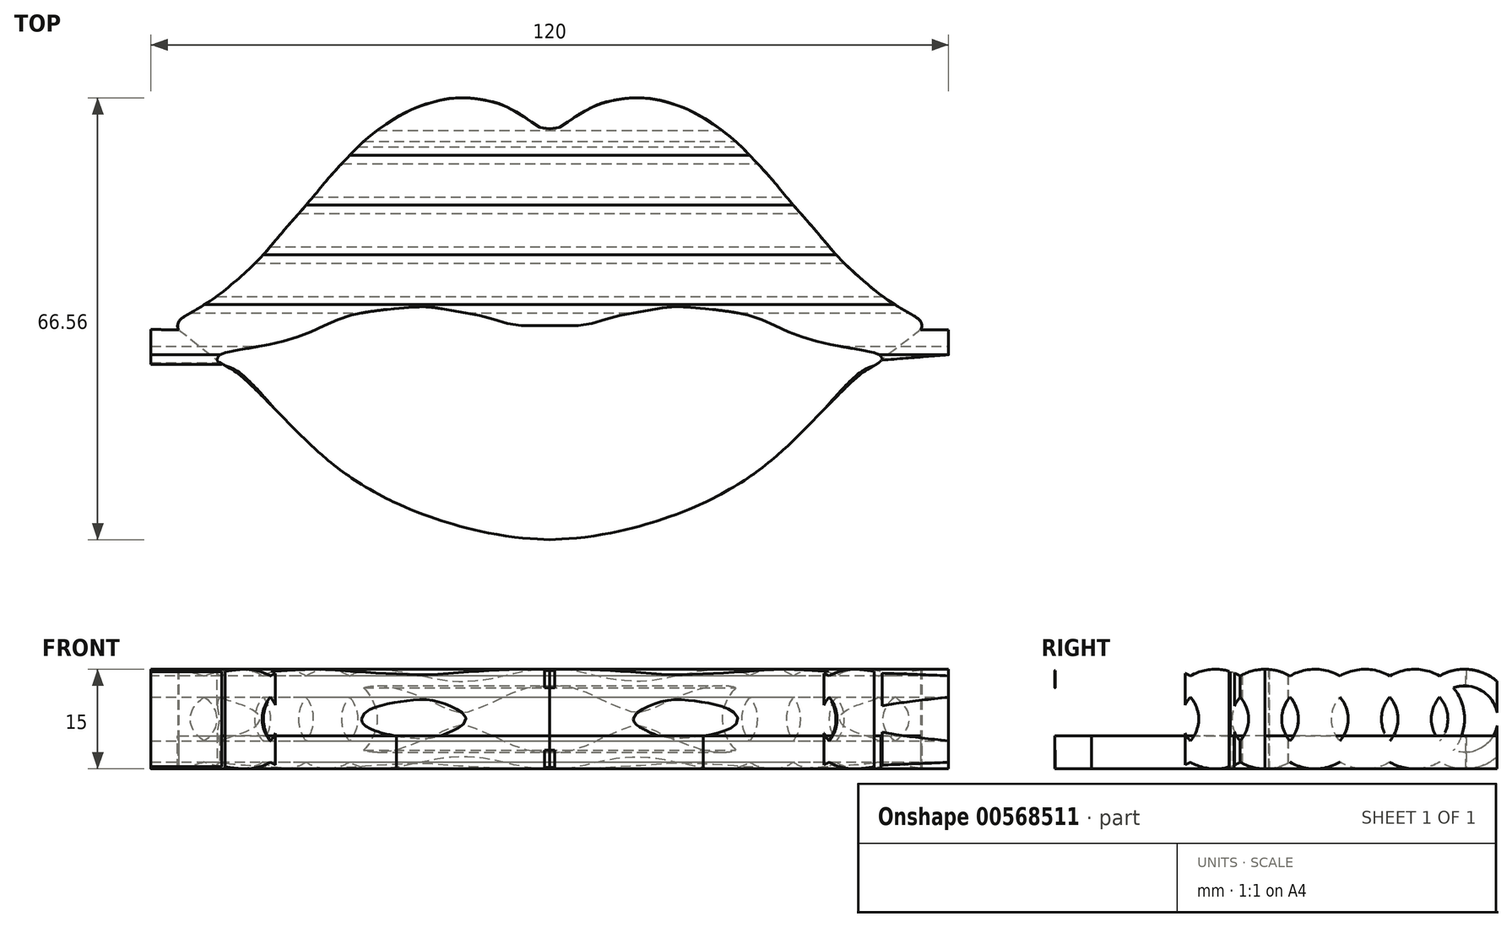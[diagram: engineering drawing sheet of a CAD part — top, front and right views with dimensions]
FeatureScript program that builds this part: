
annotation { "Feature Type Name" : "Feature", "Feature Type Description" : "" }
export const myFeature = defineFeature(function(context is Context, id is Id, definition is map)
    precondition{}
    {
        {
            var Q0;
            Q0=qCreatedBy(makeId("Right.planeOp"),FACE);
            var sketch = newSketch(context, id + "F0", { "sketchPlane" : qUnion([Q0])});
            skLineSegment(sketch, "E0", {"start": v(-15, 15) * mm, "end": v(-15, -2.5) * mm, "construction": true});
            skLineSegment(sketch, "E1", {"start": v(15, 15) * mm, "end": v(15, -2.73) * mm, "construction": true});
            skLineSegment(sketch, "E2", {"start": v(0, 0) * mm, "end": v(0, 7.5) * mm});
            skArc(sketch, "E3", {"start": v(3.75, 14) * mm, "mid": v(0, 15) * mm, "end": v(-3.75, 14) * mm});
            skArc(sketch, "E4", {"start": v(-3.75, 14) * mm, "mid": v(-7.5, 15) * mm, "end": v(-11.25, 14) * mm});
            skArc(sketch, "E5", {"start": v(1.67, 12.21) * mm, "mid": v(0, 7.5) * mm, "end": v(1.67, 2.79) * mm});
            skArc(sketch, "E6.0", {"start": v(-3.75, 10.8) * mm, "mid": v(-2.5, 7.5) * mm, "end": v(-3.75, 4.2) * mm});
            skArc(sketch, "E7.0", {"start": v(3.75, 10.8) * mm, "mid": v(5, 7.5) * mm, "end": v(3.75, 4.2) * mm});
            skArc(sketch, "E8.0", {"start": v(3.75, 10.8) * mm, "mid": v(2.5, 7.5) * mm, "end": v(3.75, 4.2) * mm});
            skArc(sketch, "E9.trimOffspring", {"start": v(1.67, 2.79) * mm, "mid": v(0, 2.5) * mm, "end": v(-1.67, 2.79) * mm});
            skArc(sketch, "E10.trimOffspring", {"start": v(5.83, 2.79) * mm, "mid": v(7.5, 7.5) * mm, "end": v(5.83, 12.21) * mm});
            skArc(sketch, "E11.trimOffspring", {"start": v(5.83, 2.79) * mm, "mid": v(7.5, 2.5) * mm, "end": v(9.17, 2.79) * mm});
            skArc(sketch, "E12.trimOffspring", {"start": v(3.75, 1) * mm, "mid": v(7.5, 0) * mm, "end": v(11.25, 1) * mm});
            skArc(sketch, "E13.trimOffspring", {"start": v(-5.83, 2.79) * mm, "mid": v(-7.5, 2.5) * mm, "end": v(-9.17, 2.79) * mm});
            skArc(sketch, "E14.trimOffspring", {"start": v(-1.67, 2.79) * mm, "mid": v(0, 7.5) * mm, "end": v(-1.67, 12.21) * mm});
            skArc(sketch, "E15.trimOffspring", {"start": v(-1.67, 12.21) * mm, "mid": v(0, 12.5) * mm, "end": v(1.67, 12.21) * mm});
            skArc(sketch, "E16.trimOffspring", {"start": v(-5.83, 12.21) * mm, "mid": v(-7.5, 7.5) * mm, "end": v(-5.83, 2.79) * mm});
            skArc(sketch, "E17.trimOffspring", {"start": v(-3.75, 4.2) * mm, "mid": v(-5, 7.5) * mm, "end": v(-3.75, 10.8) * mm});
            skArc(sketch, "E18.trimOffspring", {"start": v(-3.75, 1) * mm, "mid": v(0, 0) * mm, "end": v(3.75, 1) * mm});
            skLineSegment(sketch, "E19", {"start": v(15, 15) * mm, "end": v(36.76, 15) * mm, "construction": true});
            skLineSegment(sketch, "E20", {"start": v(35.15, 0) * mm, "end": v(35.15, 18.48) * mm, "construction": true});
            skArc(sketch, "E21", {"start": v(11.25, 1) * mm, "mid": v(15, 0) * mm, "end": v(18.75, 1) * mm});
            skArc(sketch, "E22", {"start": v(-9.17, 2.79) * mm, "mid": v(-7.5, 7.5) * mm, "end": v(-9.17, 12.21) * mm});
            skArc(sketch, "E23", {"start": v(18.75, 1) * mm, "mid": v(22.5, 0) * mm, "end": v(26.25, 1) * mm});
            skArc(sketch, "E24", {"start": v(-16.75, 2.82) * mm, "mid": v(-15.09, 7.5) * mm, "end": v(-16.75, 12.18) * mm});
            skPoint(sketch, "E24.centerSnap0", {"position": v(-23.34, 7.5) * mm});
            skArc(sketch, "E25", {"start": v(26.25, 1) * mm, "mid": v(37.5, 7.5) * mm, "end": v(26.25, 14) * mm});
            skArc(sketch, "E26.0", {"start": v(18.75, 4.2) * mm, "mid": v(20, 7.5) * mm, "end": v(18.75, 10.8) * mm});
            skArc(sketch, "E27.0", {"start": v(28.33, 2.79) * mm, "mid": v(35, 7.5) * mm, "end": v(28.33, 12.21) * mm});
            skArc(sketch, "E28.0", {"start": v(20.83, 2.79) * mm, "mid": v(22.5, 2.5) * mm, "end": v(24.17, 2.79) * mm});
            skArc(sketch, "E29.0", {"start": v(-11.25, 4.2) * mm, "mid": v(-10, 7.5) * mm, "end": v(-11.25, 10.8) * mm});
            skArc(sketch, "E30.0", {"start": v(-19.06, 4.58) * mm, "mid": v(-17.99, 7.5) * mm, "end": v(-19.06, 10.42) * mm});
            skArc(sketch, "E31.trimOffspring", {"start": v(9.17, 12.21) * mm, "mid": v(7.5, 12.5) * mm, "end": v(5.83, 12.21) * mm});
            skArc(sketch, "E32.trimOffspring", {"start": v(11.25, 4.2) * mm, "mid": v(12.5, 7.5) * mm, "end": v(11.25, 10.8) * mm});
            skArc(sketch, "E33.trimOffspring", {"start": v(9.17, 12.21) * mm, "mid": v(7.5, 7.5) * mm, "end": v(9.17, 2.79) * mm});
            skArc(sketch, "E34.trimOffspring", {"start": v(-9.17, 12.21) * mm, "mid": v(-7.5, 12.5) * mm, "end": v(-5.83, 12.21) * mm});
            skArc(sketch, "E35.trimOffspring", {"start": v(-11.25, 4.2) * mm, "mid": v(-12.5, 7.5) * mm, "end": v(-11.25, 10.8) * mm});
            skArc(sketch, "E36.trimOffspring", {"start": v(-13.33, 12.21) * mm, "mid": v(-15.05, 12.5) * mm, "end": v(-16.75, 12.18) * mm});
            skArc(sketch, "E37.trimOffspring", {"start": v(-11.25, 14) * mm, "mid": v(-15.05, 15) * mm, "end": v(-18.84, 13.95) * mm});
            skArc(sketch, "E38.trimOffspring", {"start": v(-11.25, 1) * mm, "mid": v(-7.5, 0) * mm, "end": v(-3.75, 1) * mm});
            skArc(sketch, "E39.trimOffspring", {"start": v(-13.33, 12.21) * mm, "mid": v(-15, 7.5) * mm, "end": v(-13.33, 2.79) * mm});
            skArc(sketch, "E40.trimOffspring", {"start": v(-19.06, 10.42) * mm, "mid": v(-20, 7.5) * mm, "end": v(-19.06, 4.58) * mm});
            skArc(sketch, "E41.trimOffspring", {"start": v(-16.75, 2.82) * mm, "mid": v(-15.05, 2.5) * mm, "end": v(-13.33, 2.79) * mm});
            skArc(sketch, "E42.trimOffspring", {"start": v(-21.14, 11.8) * mm, "mid": v(-22.46, 12.01) * mm, "end": v(-23.79, 11.83) * mm});
            skArc(sketch, "E43.trimOffspring", {"start": v(-18.84, 1.05) * mm, "mid": v(-15.05, 0) * mm, "end": v(-11.25, 1) * mm});
            skArc(sketch, "E44.trimOffspring", {"start": v(13.33, 2.79) * mm, "mid": v(15, 7.5) * mm, "end": v(13.33, 12.21) * mm});
            skArc(sketch, "E45.trimOffspring", {"start": v(20.83, 2.79) * mm, "mid": v(22.5, 7.5) * mm, "end": v(20.83, 12.21) * mm});
            skArc(sketch, "E46.trimOffspring", {"start": v(11.25, 10.8) * mm, "mid": v(10, 7.5) * mm, "end": v(11.25, 4.2) * mm});
            skArc(sketch, "E47.trimOffspring", {"start": v(16.67, 12.21) * mm, "mid": v(15, 12.5) * mm, "end": v(13.33, 12.21) * mm});
            skArc(sketch, "E48.trimOffspring", {"start": v(11.25, 14) * mm, "mid": v(7.5, 15) * mm, "end": v(3.75, 14) * mm});
            skArc(sketch, "E49.trimOffspring", {"start": v(16.67, 12.21) * mm, "mid": v(15, 7.5) * mm, "end": v(16.67, 2.79) * mm});
            skArc(sketch, "E50.trimOffspring", {"start": v(13.33, 2.79) * mm, "mid": v(15, 2.5) * mm, "end": v(16.67, 2.79) * mm});
            skArc(sketch, "E51.trimOffspring", {"start": v(24.17, 12.21) * mm, "mid": v(22.5, 12.5) * mm, "end": v(20.83, 12.21) * mm});
            skArc(sketch, "E52.trimOffspring", {"start": v(24.17, 12.21) * mm, "mid": v(22.5, 7.5) * mm, "end": v(24.17, 2.79) * mm});
            skArc(sketch, "E53.trimOffspring", {"start": v(18.75, 14) * mm, "mid": v(15, 15) * mm, "end": v(11.25, 14) * mm});
            skArc(sketch, "E54.trimOffspring", {"start": v(18.75, 10.8) * mm, "mid": v(17.5, 7.5) * mm, "end": v(18.75, 4.2) * mm});
            skArc(sketch, "E55.trimOffspring", {"start": v(26.25, 4.2) * mm, "mid": v(27.5, 7.5) * mm, "end": v(26.25, 10.8) * mm});
            skArc(sketch, "E56.trimOffspring", {"start": v(28.33, 2.79) * mm, "mid": v(30, 7.5) * mm, "end": v(28.33, 12.21) * mm});
            skArc(sketch, "E57.trimOffspring", {"start": v(26.25, 10.8) * mm, "mid": v(25, 7.5) * mm, "end": v(26.25, 4.2) * mm});
            skArc(sketch, "E58.trimOffspring", {"start": v(26.25, 14) * mm, "mid": v(22.5, 15) * mm, "end": v(18.75, 14) * mm});
            skArc(sketch, "E59.trimOffspring", {"start": v(-21.14, 11.8) * mm, "mid": v(-22.5, 7.5) * mm, "end": v(-21.14, 3.2) * mm});
            skArc(sketch, "E60.trimOffspring", {"start": v(-18.84, 13.95) * mm, "mid": v(-22.47, 14.91) * mm, "end": v(-26.12, 13.97) * mm});
            skArc(sketch, "E61", {"start": v(-26.12, 13.97) * mm, "mid": v(-37.41, 7.5) * mm, "end": v(-26.12, 1.03) * mm});
            skArc(sketch, "E62.0", {"start": v(-25.9, 4.53) * mm, "mid": v(-24.91, 7.5) * mm, "end": v(-25.9, 10.47) * mm});
            skArc(sketch, "E63.trimOffspring", {"start": v(-25.9, 10.47) * mm, "mid": v(-27.01, 7.5) * mm, "end": v(-25.9, 4.53) * mm});
            skArc(sketch, "E64.trimOffspring", {"start": v(-28.23, 12.2) * mm, "mid": v(-29.91, 7.5) * mm, "end": v(-28.23, 2.8) * mm});
            skArc(sketch, "E65.trimOffspring", {"start": v(-23.79, 3.17) * mm, "mid": v(-22.46, 2.99) * mm, "end": v(-21.14, 3.2) * mm});
            skArc(sketch, "E66.trimOffspring", {"start": v(-23.79, 3.17) * mm, "mid": v(-22.41, 7.5) * mm, "end": v(-23.79, 11.83) * mm});
            skArc(sketch, "E67.trimOffspring", {"start": v(-26.12, 1.03) * mm, "mid": v(-22.47, 0.09) * mm, "end": v(-18.84, 1.05) * mm});
            skArc(sketch, "E68.trimOffspring", {"start": v(-28.23, 12.2) * mm, "mid": v(-34.91, 7.5) * mm, "end": v(-28.23, 2.8) * mm});
            skSolve(sketch);
        }
        {
            var Q0;
            Q0=qCreatedBy(makeId("Right.planeOp"),FACE);
            var sketch = newSketch(context, id + "F1", { "sketchPlane" : qUnion([Q0])});
            skLineSegment(sketch, "E69.bottom", {"start": v(38.2, 15.43) * mm, "end": v(-37.62, 15.43) * mm});
            skLineSegment(sketch, "E69.top", {"start": v(38.2, 0) * mm, "end": v(-37.62, 0) * mm});
            skLineSegment(sketch, "E69.left", {"start": v(38.2, 15.43) * mm, "end": v(38.2, 0) * mm});
            skLineSegment(sketch, "E69.right", {"start": v(-37.62, 15.43) * mm, "end": v(-37.62, 0) * mm});
            skSolve(sketch);
        }
        {
            var Q0;
            Q0 = qSketchRegion(id + "F1", true);
            extrude(context, id + "F2", {"entities" : qUnion([Q0]), "endBound" : BoundingType.SYMMETRIC, "depth" : 120 * mm, "offsetDistance" : 25 * mm});
        }
        {
            var Q0;
            Q0=makeQuery(id+"F2.opExtrude","CAP_FACE",FACE,{"disambiguationData":[OSD([sQuery(id+"F1.wireOp",EDGE,"E69.bottom"),sQuery(id+"F1.wireOp",EDGE,"E69.top"),sQuery(id+"F1.wireOp",EDGE,"E69.left"),sQuery(id+"F1.wireOp",EDGE,"E69.right")])],"isStart":true});
            var sketch = newSketch(context, id + "F3", { "sketchPlane" : qUnion([Q0])});
            skArc(sketch, "E70.0", {"start": v(-37.5, 7.5) * mm, "mid": v(-33.75, 14) * mm, "end": v(-26.25, 14) * mm});
            skArc(sketch, "E71.0", {"start": v(-26.25, 14) * mm, "mid": v(-22.5, 15) * mm, "end": v(-18.75, 14) * mm});
            skArc(sketch, "E72.0", {"start": v(-18.75, 14) * mm, "mid": v(-15, 15) * mm, "end": v(-11.25, 14) * mm});
            skArc(sketch, "E73.0", {"start": v(-11.25, 14) * mm, "mid": v(-7.5, 15) * mm, "end": v(-3.75, 14) * mm});
            skArc(sketch, "E74.0", {"start": v(-3.75, 14) * mm, "mid": v(0, 15) * mm, "end": v(3.75, 14) * mm});
            skArc(sketch, "E75.0", {"start": v(3.75, 14) * mm, "mid": v(7.5, 15) * mm, "end": v(11.25, 14) * mm});
            skArc(sketch, "E76.0", {"start": v(11.25, 14) * mm, "mid": v(15.05, 15) * mm, "end": v(18.84, 13.95) * mm});
            skArc(sketch, "E77.0", {"start": v(18.84, 13.95) * mm, "mid": v(22.47, 14.91) * mm, "end": v(26.12, 13.97) * mm});
            skArc(sketch, "E78.0", {"start": v(26.12, 13.97) * mm, "mid": v(33.55, 14.06) * mm, "end": v(37.41, 7.72) * mm});
            skLineSegment(sketch, "E79", {"start": v(-38.2, 21.5) * mm, "end": v(37.62, 21.5) * mm});
            skLineSegment(sketch, "E80", {"start": v(37.62, 21.5) * mm, "end": v(37.62, 7.72) * mm});
            skLineSegment(sketch, "E81", {"start": v(-37.5, 7.5) * mm, "end": v(-38.2, 7.5) * mm});
            skLineSegment(sketch, "E82", {"start": v(-38.2, 7.5) * mm, "end": v(-38.2, 21.5) * mm});
            skPoint(sketch, "E83.orphan", {"position": v(-26.25, 1) * mm});
            skPoint(sketch, "E84.0.start.orphan", {"position": v(-18.75, 1) * mm});
            skPoint(sketch, "E85.0.start.orphan", {"position": v(-11.25, 1) * mm});
            skPoint(sketch, "E86.0.start.orphan", {"position": v(-3.75, 1) * mm});
            skPoint(sketch, "E87.0.start.orphan", {"position": v(3.75, 1) * mm});
            skPoint(sketch, "E88.0.start.orphan", {"position": v(11.25, 1) * mm});
            skPoint(sketch, "E89.0.start.orphan", {"position": v(18.84, 1.05) * mm});
            skPoint(sketch, "E90.0.start.orphan", {"position": v(26.12, 1.03) * mm});
            skLineSegment(sketch, "E91", {"start": v(37.62, 7.72) * mm, "end": v(37.41, 7.72) * mm});
            skSolve(sketch);
        }
        {
            var Q0;
            Q0 = qSketchRegion(id + "F3", true);
            extrude(context, id + "F4", {"entities" : qUnion([Q0]), "operationType" : NewBodyOperationType.REMOVE, "endBound" : BoundingType.THROUGH_ALL, "oppositeDirection" : true, "depth" : 25 * mm, "offsetDistance" : 25 * mm});
        }
        {
            var Q0;
            Q0=makeQuery(id+"F2.opExtrude","CAP_FACE",FACE,{"disambiguationData":[OSD([sQuery(id+"F1.wireOp",EDGE,"E69.bottom"),sQuery(id+"F1.wireOp",EDGE,"E69.top"),sQuery(id+"F1.wireOp",EDGE,"E69.left"),sQuery(id+"F1.wireOp",EDGE,"E69.right")])],"isStart":false});
            var sketch = newSketch(context, id + "F5", { "sketchPlane" : qUnion([Q0])});
            skArc(sketch, "E92.0", {"start": v(-37.41, 7.72) * mm, "mid": v(-33.74, 1.05) * mm, "end": v(-26.12, 1.03) * mm});
            skArc(sketch, "E92.1", {"start": v(-26.12, 1.03) * mm, "mid": v(-22.47, 0.09) * mm, "end": v(-18.84, 1.05) * mm});
            skArc(sketch, "E92.2", {"start": v(-18.84, 1.05) * mm, "mid": v(-15.05, 0) * mm, "end": v(-11.25, 1) * mm});
            skArc(sketch, "E92.3", {"start": v(-11.25, 1) * mm, "mid": v(-7.5, 0) * mm, "end": v(-3.75, 1) * mm});
            skArc(sketch, "E92.4", {"start": v(-3.75, 1) * mm, "mid": v(0, 0) * mm, "end": v(3.75, 1) * mm});
            skPoint(sketch, "E92.5", {"position": v(5.55, 0) * mm});
            skArc(sketch, "E92.6", {"start": v(3.75, 1) * mm, "mid": v(7.5, 0) * mm, "end": v(11.25, 1) * mm});
            skArc(sketch, "E92.7", {"start": v(11.25, 1) * mm, "mid": v(15, 0) * mm, "end": v(18.75, 1) * mm});
            skArc(sketch, "E92.8", {"start": v(18.75, 1) * mm, "mid": v(22.5, 0) * mm, "end": v(26.25, 1) * mm});
            skArc(sketch, "E92.9", {"start": v(26.25, 1) * mm, "mid": v(33.75, 1) * mm, "end": v(37.5, 7.5) * mm});
            skLineSegment(sketch, "E92.10", {"start": v(38.2, 7.5) * mm, "end": v(37.5, 7.5) * mm});
            skLineSegment(sketch, "E92.11", {"start": v(38.2, 7.5) * mm, "end": v(38.2, 0) * mm});
            skLineSegment(sketch, "E92.12", {"start": v(-37.62, 7.72) * mm, "end": v(-37.62, 0) * mm});
            skPoint(sketch, "E92.13", {"position": v(-37.52, 7.72) * mm});
            skLineSegment(sketch, "E93", {"start": v(-37.62, 7.72) * mm, "end": v(-37.41, 7.72) * mm});
            skPoint(sketch, "E94.orphan", {"position": v(-26.12, 13.97) * mm});
            skPoint(sketch, "E95.orphan", {"position": v(26.25, 14) * mm});
            skLineSegment(sketch, "E96", {"start": v(38.2, 0) * mm, "end": v(38.2, -4.66) * mm});
            skLineSegment(sketch, "E97", {"start": v(38.2, -4.66) * mm, "end": v(-37.95, -4.66) * mm});
            skLineSegment(sketch, "E98", {"start": v(-37.95, -4.66) * mm, "end": v(-37.62, 0) * mm});
            skSolve(sketch);
        }
        {
            var Q0;
            Q0 = qSketchRegion(id + "F5", true);
            extrude(context, id + "F6", {"entities" : qUnion([Q0]), "operationType" : NewBodyOperationType.REMOVE, "endBound" : BoundingType.THROUGH_ALL, "oppositeDirection" : true, "depth" : 25 * mm, "offsetDistance" : 25 * mm});
        }
        {
            var Q0;
            Q0=qCreatedBy(makeId("Right.planeOp"),FACE);
            var sketch = newSketch(context, id + "F7", { "sketchPlane" : qUnion([Q0])});
            skArc(sketch, "E99.0", {"start": v(-28.23, 12.2) * mm, "mid": v(-34.91, 7.5) * mm, "end": v(-28.23, 2.8) * mm});
            skArc(sketch, "E99.1", {"start": v(-28.23, 12.2) * mm, "mid": v(-29.91, 7.5) * mm, "end": v(-28.23, 2.8) * mm});
            skArc(sketch, "E99.2", {"start": v(-25.9, 10.47) * mm, "mid": v(-27.01, 7.5) * mm, "end": v(-25.9, 4.53) * mm});
            skArc(sketch, "E99.3", {"start": v(-25.9, 4.53) * mm, "mid": v(-24.91, 7.5) * mm, "end": v(-25.9, 10.47) * mm});
            skArc(sketch, "E99.4", {"start": v(-19.06, 10.42) * mm, "mid": v(-20, 7.5) * mm, "end": v(-19.06, 4.58) * mm});
            skArc(sketch, "E99.5", {"start": v(-19.06, 4.58) * mm, "mid": v(-17.99, 7.5) * mm, "end": v(-19.06, 10.42) * mm});
            skArc(sketch, "E99.6", {"start": v(-11.25, 4.2) * mm, "mid": v(-12.5, 7.5) * mm, "end": v(-11.25, 10.8) * mm});
            skArc(sketch, "E99.7", {"start": v(-11.25, 4.2) * mm, "mid": v(-10, 7.5) * mm, "end": v(-11.25, 10.8) * mm});
            skArc(sketch, "E99.8", {"start": v(-3.75, 4.2) * mm, "mid": v(-5, 7.5) * mm, "end": v(-3.75, 10.8) * mm});
            skArc(sketch, "E99.9", {"start": v(-3.75, 10.8) * mm, "mid": v(-2.5, 7.5) * mm, "end": v(-3.75, 4.2) * mm});
            skArc(sketch, "E99.10", {"start": v(3.75, 10.8) * mm, "mid": v(2.5, 7.5) * mm, "end": v(3.75, 4.2) * mm});
            skArc(sketch, "E99.11", {"start": v(3.75, 10.8) * mm, "mid": v(5, 7.5) * mm, "end": v(3.75, 4.2) * mm});
            skArc(sketch, "E99.12", {"start": v(11.25, 10.8) * mm, "mid": v(10, 7.5) * mm, "end": v(11.25, 4.2) * mm});
            skArc(sketch, "E99.13", {"start": v(11.25, 4.2) * mm, "mid": v(12.5, 7.5) * mm, "end": v(11.25, 10.8) * mm});
            skArc(sketch, "E99.14", {"start": v(18.75, 10.8) * mm, "mid": v(17.5, 7.5) * mm, "end": v(18.75, 4.2) * mm});
            skArc(sketch, "E99.15", {"start": v(18.75, 4.2) * mm, "mid": v(20, 7.5) * mm, "end": v(18.75, 10.8) * mm});
            skArc(sketch, "E99.16", {"start": v(26.25, 10.8) * mm, "mid": v(25, 7.5) * mm, "end": v(26.25, 4.2) * mm});
            skArc(sketch, "E99.17", {"start": v(26.25, 4.2) * mm, "mid": v(27.5, 7.5) * mm, "end": v(26.25, 10.8) * mm});
            skArc(sketch, "E99.18", {"start": v(28.33, 2.79) * mm, "mid": v(30, 7.5) * mm, "end": v(28.33, 12.21) * mm});
            skArc(sketch, "E99.19", {"start": v(28.33, 2.79) * mm, "mid": v(35, 7.5) * mm, "end": v(28.33, 12.21) * mm});
            skPoint(sketch, "E99.20", {"position": v(-5, 7.5) * mm});
            skPoint(sketch, "E99.21", {"position": v(2.5, 7.5) * mm});
            skSolve(sketch);
        }
        {
            var Q0;
            Q0 = qSketchRegion(id + "F7", true);
            extrude(context, id + "F8", {"entities" : qUnion([Q0]), "operationType" : NewBodyOperationType.REMOVE, "endBound" : BoundingType.SYMMETRIC, "oppositeDirection" : true, "depth" : 120 * mm, "offsetDistance" : 25 * mm});
        }
        {
            var Q0;
            Q0=makeQuery(id+"F2.opExtrude","CAP_FACE",FACE,{"disambiguationData":[OSD([sQuery(id+"F1.wireOp",EDGE,"E69.bottom"),sQuery(id+"F1.wireOp",EDGE,"E69.top"),sQuery(id+"F1.wireOp",EDGE,"E69.left"),sQuery(id+"F1.wireOp",EDGE,"E69.right")])],"isStart":false});
            var sketch = newSketch(context, id + "F9", { "sketchPlane" : qUnion([Q0])});
            skArc(sketch, "E100.0", {"start": v(-21.14, 11.8) * mm, "mid": v(-22.46, 12.01) * mm, "end": v(-23.79, 11.83) * mm});
            skArc(sketch, "E100.1", {"start": v(-21.14, 11.8) * mm, "mid": v(-22.02, 10.14) * mm, "end": v(-22.46, 8.3) * mm});
            skArc(sketch, "E100.2", {"start": v(-23.79, 3.17) * mm, "mid": v(-22.9, 4.85) * mm, "end": v(-22.46, 6.7) * mm});
            skArc(sketch, "E100.3", {"start": v(-23.79, 3.17) * mm, "mid": v(-22.46, 2.99) * mm, "end": v(-21.14, 3.2) * mm});
            skArc(sketch, "E101.trimOffspring", {"start": v(-22.46, 8.3) * mm, "mid": v(-22.9, 10.15) * mm, "end": v(-23.79, 11.83) * mm});
            skArc(sketch, "E102.trimOffspring", {"start": v(-22.46, 6.7) * mm, "mid": v(-22.02, 4.86) * mm, "end": v(-21.14, 3.2) * mm});
            skSolve(sketch);
        }
        {
            var Q0;
            Q0=qCreatedBy(makeId("Right.planeOp"),FACE);
            var sketch = newSketch(context, id + "F10", { "sketchPlane" : qUnion([Q0])});
            skPoint(sketch, "E103.0", {"position": v(-22.46, 12.01) * mm});
            skArc(sketch, "E104.0", {"start": v(-13.33, 12.21) * mm, "mid": v(-14.43, 10.38) * mm, "end": v(-14.96, 8.3) * mm});
            skArc(sketch, "E105.0", {"start": v(-13.33, 12.21) * mm, "mid": v(-15.05, 12.5) * mm, "end": v(-16.75, 12.18) * mm});
            skArc(sketch, "E106.0", {"start": v(-16.75, 2.82) * mm, "mid": v(-15.63, 4.7) * mm, "end": v(-15.12, 6.84) * mm});
            skArc(sketch, "E107.0", {"start": v(-5.83, 12.21) * mm, "mid": v(-6.93, 10.38) * mm, "end": v(-7.46, 8.3) * mm});
            skArc(sketch, "E108.0", {"start": v(-9.17, 2.79) * mm, "mid": v(-8.05, 4.7) * mm, "end": v(-7.53, 6.84) * mm});
            skArc(sketch, "E109.0", {"start": v(-9.17, 12.21) * mm, "mid": v(-7.5, 12.5) * mm, "end": v(-5.83, 12.21) * mm});
            skArc(sketch, "E110.0", {"start": v(-5.83, 2.79) * mm, "mid": v(-7.5, 2.5) * mm, "end": v(-9.17, 2.79) * mm});
            skArc(sketch, "E111.0", {"start": v(-16.75, 2.82) * mm, "mid": v(-15.05, 2.5) * mm, "end": v(-13.33, 2.79) * mm});
            skArc(sketch, "E112.0", {"start": v(1.67, 2.79) * mm, "mid": v(0, 2.5) * mm, "end": v(-1.67, 2.79) * mm});
            skArc(sketch, "E113.0", {"start": v(1.67, 12.21) * mm, "mid": v(0.57, 10.38) * mm, "end": v(0.04, 8.3) * mm});
            skArc(sketch, "E114.0", {"start": v(-1.67, 2.79) * mm, "mid": v(-0.55, 4.7) * mm, "end": v(-0.03, 6.84) * mm});
            skArc(sketch, "E115.0", {"start": v(-1.67, 12.21) * mm, "mid": v(0, 12.5) * mm, "end": v(1.67, 12.21) * mm});
            skArc(sketch, "E116.0", {"start": v(5.83, 2.79) * mm, "mid": v(6.95, 4.7) * mm, "end": v(7.47, 6.84) * mm});
            skArc(sketch, "E117.0", {"start": v(9.17, 12.21) * mm, "mid": v(8.07, 10.38) * mm, "end": v(7.54, 8.3) * mm});
            skPoint(sketch, "E118.0", {"position": v(7.5, 12.5) * mm});
            skArc(sketch, "E119.0", {"start": v(9.17, 12.21) * mm, "mid": v(7.5, 12.5) * mm, "end": v(5.83, 12.21) * mm});
            skArc(sketch, "E120.0", {"start": v(5.83, 2.79) * mm, "mid": v(7.5, 2.5) * mm, "end": v(9.17, 2.79) * mm});
            skArc(sketch, "E121.0", {"start": v(13.33, 2.79) * mm, "mid": v(15, 2.5) * mm, "end": v(16.67, 2.79) * mm});
            skArc(sketch, "E122.0", {"start": v(16.67, 12.21) * mm, "mid": v(15.57, 10.38) * mm, "end": v(15.04, 8.3) * mm});
            skArc(sketch, "E123.0", {"start": v(13.33, 2.79) * mm, "mid": v(14.45, 4.7) * mm, "end": v(14.97, 6.84) * mm});
            skArc(sketch, "E124.0", {"start": v(16.67, 12.21) * mm, "mid": v(15, 12.5) * mm, "end": v(13.33, 12.21) * mm});
            skArc(sketch, "E125.0", {"start": v(20.83, 2.79) * mm, "mid": v(21.95, 4.7) * mm, "end": v(22.47, 6.84) * mm});
            skArc(sketch, "E126.0", {"start": v(24.17, 12.21) * mm, "mid": v(23.07, 10.38) * mm, "end": v(22.54, 8.3) * mm});
            skArc(sketch, "E127.0", {"start": v(24.17, 12.21) * mm, "mid": v(22.5, 12.5) * mm, "end": v(20.83, 12.21) * mm});
            skPoint(sketch, "E128.0", {"position": v(22.5, 2.5) * mm});
            skArc(sketch, "E129.0", {"start": v(20.83, 2.79) * mm, "mid": v(22.5, 2.5) * mm, "end": v(24.17, 2.79) * mm});
            skArc(sketch, "E130.0", {"start": v(-23.79, 3.17) * mm, "mid": v(-22.46, 2.99) * mm, "end": v(-21.14, 3.2) * mm});
            skLineSegment(sketch, "E131", {"start": v(22.5, 7.5) * mm, "end": v(-39, 7.5) * mm, "construction": true});
            skLineSegment(sketch, "E132", {"start": v(-15.13, 8.3) * mm, "end": v(-14.96, 8.3) * mm});
            skLineSegment(sketch, "E133", {"start": v(-15.12, 6.84) * mm, "end": v(-14.97, 6.84) * mm});
            skArc(sketch, "E134.trimOffspring", {"start": v(22.46, 8.3) * mm, "mid": v(21.93, 10.38) * mm, "end": v(20.83, 12.21) * mm});
            skArc(sketch, "E135.trimOffspring", {"start": v(22.53, 6.84) * mm, "mid": v(23.05, 4.7) * mm, "end": v(24.17, 2.79) * mm});
            skArc(sketch, "E136.trimOffspring", {"start": v(15.03, 6.84) * mm, "mid": v(15.55, 4.7) * mm, "end": v(16.67, 2.79) * mm});
            skArc(sketch, "E137.trimOffspring", {"start": v(14.96, 8.3) * mm, "mid": v(14.43, 10.38) * mm, "end": v(13.33, 12.21) * mm});
            skArc(sketch, "E138.trimOffspring", {"start": v(7.53, 6.84) * mm, "mid": v(8.05, 4.7) * mm, "end": v(9.17, 2.79) * mm});
            skArc(sketch, "E139.trimOffspring", {"start": v(7.46, 8.3) * mm, "mid": v(6.93, 10.38) * mm, "end": v(5.83, 12.21) * mm});
            skArc(sketch, "E140.trimOffspring", {"start": v(-0.04, 8.3) * mm, "mid": v(-0.57, 10.38) * mm, "end": v(-1.67, 12.21) * mm});
            skArc(sketch, "E141.trimOffspring", {"start": v(0.03, 6.84) * mm, "mid": v(0.55, 4.7) * mm, "end": v(1.67, 2.79) * mm});
            skArc(sketch, "E142.trimOffspring", {"start": v(-7.54, 8.3) * mm, "mid": v(-8.07, 10.38) * mm, "end": v(-9.17, 12.21) * mm});
            skArc(sketch, "E143.trimOffspring", {"start": v(-7.47, 6.84) * mm, "mid": v(-6.95, 4.7) * mm, "end": v(-5.83, 2.79) * mm});
            skArc(sketch, "E144.trimOffspring", {"start": v(-15.13, 8.3) * mm, "mid": v(-15.66, 10.36) * mm, "end": v(-16.75, 12.18) * mm});
            skArc(sketch, "E145.trimOffspring", {"start": v(-14.97, 6.84) * mm, "mid": v(-14.45, 4.7) * mm, "end": v(-13.33, 2.79) * mm});
            skLineSegment(sketch, "E146.trimOffspring", {"start": v(-7.54, 8.3) * mm, "end": v(-7.46, 8.3) * mm});
            skLineSegment(sketch, "E147.trimOffspring", {"start": v(-7.53, 6.84) * mm, "end": v(-7.47, 6.84) * mm});
            skLineSegment(sketch, "E148.trimOffspring", {"start": v(-0.03, 6.84) * mm, "end": v(0.03, 6.84) * mm});
            skLineSegment(sketch, "E149.trimOffspring", {"start": v(-0.04, 8.3) * mm, "end": v(0.04, 8.3) * mm});
            skLineSegment(sketch, "E150.trimOffspring", {"start": v(7.46, 8.3) * mm, "end": v(7.54, 8.3) * mm});
            skLineSegment(sketch, "E151.trimOffspring", {"start": v(7.47, 6.84) * mm, "end": v(7.53, 6.84) * mm});
            skLineSegment(sketch, "E152.trimOffspring", {"start": v(14.96, 8.3) * mm, "end": v(15.04, 8.3) * mm});
            skLineSegment(sketch, "E153.trimOffspring", {"start": v(14.97, 6.84) * mm, "end": v(15.03, 6.84) * mm});
            skLineSegment(sketch, "E154.trimOffspring", {"start": v(22.47, 6.84) * mm, "end": v(22.53, 6.84) * mm});
            skLineSegment(sketch, "E155.trimOffspring", {"start": v(22.46, 8.3) * mm, "end": v(22.54, 8.3) * mm});
            skPoint(sketch, "E156.orphan", {"position": v(39.08, 8.3) * mm});
            skPoint(sketch, "E157.orphan", {"position": v(39.08, 6.84) * mm});
            skPoint(sketch, "E158.0.end.orphan", {"position": v(-22.46, 8.3) * mm});
            skPoint(sketch, "E158.0.start.orphan", {"position": v(-21.14, 11.8) * mm});
            skSolve(sketch);
        }
        {
            var Q0;
            Q0 = qSketchRegion(id + "F9", true);
            extrude(context, id + "F11", {"entities" : qUnion([Q0]), "operationType" : NewBodyOperationType.REMOVE, "endBound" : BoundingType.THROUGH_ALL, "oppositeDirection" : true, "depth" : 25 * mm, "offsetDistance" : 25 * mm});
        }
        {
            var Q0;
            Q0=qCreatedBy(makeId("Top.planeOp"),FACE);
            var sketch = newSketch(context, id + "F12", { "sketchPlane" : qUnion([Q0])});
            skFitSpline(sketch, "E159", {"points": [v(-48.78, -3.43) * mm, v(-41.24, -1.85) * mm, v(-35.4, 0) * mm, v(-31.38, 1.56) * mm, v(-26.75, 2.66) * mm, v(-21.4, 3.26) * mm, v(-17.74, 3.26) * mm, v(-14.34, 2.78) * mm, v(-10.56, 2.05) * mm, v(-6.79, 1.07) * mm, v(-5.15, 0.73) * mm, v(-2.98, 0.59) * mm, v(-0.95, 0.6) * mm, v(0, 0.6) * mm], "startDerivative": vector(68.72, 12.95) * mm, "endDerivative": vector(20.26, 1.64) * mm, "construction": true});
            skLineSegment(sketch, "E160", {"start": v(0, 0.6) * mm, "end": v(0, -31.65) * mm});
            skFitSpline(sketch, "E161", {"points": [v(0, -31.65) * mm, v(-2.89, -31.43) * mm, v(-6.74, -31) * mm, v(-12.4, -29.88) * mm, v(-20.63, -27.18) * mm, v(-27.93, -23.53) * mm, v(-34.38, -18.79) * mm, v(-41.81, -11.48) * mm, v(-47.17, -6.43) * mm, v(-49.17, -5.21) * mm, v(-49.84, -4.6) * mm, v(-49.66, -4) * mm, v(-48.78, -3.43) * mm], "startDerivative": vector(-41.12, 3.01) * mm, "endDerivative": vector(24.6, 12.04) * mm});
            skFitSpline(sketch, "E162.MirrorCS", {"points": [v(0, -31.65) * mm, v(2.89, -31.43) * mm, v(6.74, -31) * mm, v(12.4, -29.88) * mm, v(20.63, -27.18) * mm, v(27.93, -23.53) * mm, v(34.38, -18.79) * mm, v(41.81, -11.48) * mm, v(47.17, -6.43) * mm, v(49.17, -5.21) * mm, v(49.84, -4.6) * mm, v(49.66, -4) * mm, v(48.78, -3.43) * mm], "startDerivative": vector(41.12, 3.01) * mm, "endDerivative": vector(-24.6, 12.04) * mm});
            skFitSpline(sketch, "E163.MirrorCS", {"points": [v(48.78, -3.43) * mm, v(41.24, -1.85) * mm, v(35.4, 0) * mm, v(31.38, 1.56) * mm, v(26.75, 2.66) * mm, v(21.4, 3.26) * mm, v(17.74, 3.26) * mm, v(14.34, 2.78) * mm, v(10.56, 2.05) * mm, v(6.79, 1.07) * mm, v(5.15, 0.73) * mm, v(2.98, 0.59) * mm, v(0.95, 0.6) * mm, v(0, 0.6) * mm], "startDerivative": vector(-68.72, 12.95) * mm, "endDerivative": vector(-20.26, 1.64) * mm});
            skFitSpline(sketch, "E164.MirrorCS", {"points": [v(0, -31.65) * mm, v(2.89, -31.43) * mm, v(6.74, -31) * mm, v(12.4, -29.88) * mm, v(20.63, -27.18) * mm, v(27.93, -23.53) * mm, v(34.38, -18.79) * mm, v(41.81, -11.48) * mm, v(47.17, -6.43) * mm, v(49.17, -5.21) * mm, v(49.84, -4.6) * mm, v(49.66, -4) * mm, v(48.78, -3.43) * mm], "startDerivative": vector(41.12, 3.01) * mm, "endDerivative": vector(-24.6, 12.04) * mm});
            skLineSegment(sketch, "E165", {"start": v(-49.17, -5.21) * mm, "end": v(-68.23, -5.21) * mm});
            skLineSegment(sketch, "E166", {"start": v(-68.23, -5.21) * mm, "end": v(-68.23, -54.34) * mm});
            skLineSegment(sketch, "E167", {"start": v(-68.23, -54.34) * mm, "end": v(71.1, -54.34) * mm});
            skLineSegment(sketch, "E168", {"start": v(71.1, -54.34) * mm, "end": v(71.1, -2.88) * mm});
            skLineSegment(sketch, "E169", {"start": v(71.1, -2.88) * mm, "end": v(49.84, -4.6) * mm});
            skSolve(sketch);
        }
        {
            var Q0;
            Q0=qCreatedBy(makeId("Top.planeOp"),FACE);
            var sketch = newSketch(context, id + "F13", { "sketchPlane" : qUnion([Q0])});
            skFitSpline(sketch, "E170", {"points": [v(-55.86, 0) * mm, v(-53.62, -0.77) * mm, v(-50.44, 0) * mm, v(-43.21, 2.85) * mm, v(-36.25, 6.57) * mm, v(-30.37, 10.18) * mm, v(-23.5, 12.77) * mm, v(-16.98, 13.32) * mm, v(-11.72, 12.5) * mm, v(-8.09, 10.87) * mm, v(-5.82, 9.96) * mm, v(-2.83, 9.33) * mm, v(0, 9.15) * mm], "startDerivative": vector(37.57, -18.17) * mm, "endDerivative": vector(43.07, -1.33) * mm, "construction": true});
            skLineSegment(sketch, "E171", {"start": v(0, 9.15) * mm, "end": v(0, 30.25) * mm});
            skFitSpline(sketch, "E172", {"points": [v(0, 30.25) * mm, v(-0.8, 30.25) * mm, v(-1.96, 30.73) * mm, v(-3.98, 32.14) * mm, v(-5.7, 33.14) * mm, v(-7.47, 33.97) * mm, v(-9.04, 34.42) * mm, v(-11.1, 34.77) * mm, v(-12.76, 34.9) * mm, v(-14.24, 34.87) * mm, v(-16.1, 34.64) * mm, v(-18.4, 34.03) * mm, v(-20.08, 33.46) * mm, v(-23.03, 31.95) * mm, v(-27.45, 28.8) * mm, v(-30.6, 25.73) * mm, v(-33.2, 22.9) * mm, v(-36.34, 19.12) * mm, v(-39.32, 15.72) * mm, v(-41.76, 12.83) * mm, v(-43.9, 10.43) * mm, v(-46.6, 7.9) * mm, v(-49.39, 5.55) * mm, v(-51.41, 4.11) * mm, v(-53.75, 2.7) * mm, v(-54.87, 2.03) * mm, v(-55.74, 1.32) * mm, v(-55.98, 0.56) * mm, v(-55.83, -0.02) * mm], "startDerivative": vector(-37.81, -3.2) * mm, "endDerivative": vector(17.07, -29.9) * mm});
            skFitSpline(sketch, "E173.MirrorCS", {"points": [v(55.86, 0) * mm, v(53.62, -0.77) * mm, v(50.44, 0) * mm, v(43.21, 2.85) * mm, v(36.25, 6.57) * mm, v(30.37, 10.18) * mm, v(23.5, 12.77) * mm, v(16.98, 13.32) * mm, v(11.72, 12.5) * mm, v(8.09, 10.87) * mm, v(5.82, 9.96) * mm, v(2.83, 9.33) * mm, v(0, 9.15) * mm], "startDerivative": vector(-37.57, -18.17) * mm, "endDerivative": vector(-43.07, -1.33) * mm, "construction": true});
            skFitSpline(sketch, "E174.MirrorCS", {"points": [v(0, 30.25) * mm, v(0.8, 30.25) * mm, v(1.96, 30.73) * mm, v(3.98, 32.14) * mm, v(5.7, 33.14) * mm, v(7.47, 33.97) * mm, v(9.04, 34.42) * mm, v(11.1, 34.77) * mm, v(12.76, 34.9) * mm, v(14.24, 34.87) * mm, v(16.1, 34.64) * mm, v(18.4, 34.03) * mm, v(20.08, 33.46) * mm, v(23.03, 31.95) * mm, v(27.45, 28.8) * mm, v(30.6, 25.73) * mm, v(33.2, 22.9) * mm, v(36.34, 19.12) * mm, v(39.32, 15.72) * mm, v(41.76, 12.83) * mm, v(43.9, 10.43) * mm, v(46.6, 7.9) * mm, v(49.39, 5.55) * mm, v(51.41, 4.11) * mm, v(53.75, 2.7) * mm, v(54.87, 2.03) * mm, v(55.74, 1.32) * mm, v(55.98, 0.56) * mm, v(55.83, -0.02) * mm], "startDerivative": vector(37.81, -3.2) * mm, "endDerivative": vector(-17.07, -29.9) * mm});
            skLineSegment(sketch, "E175", {"start": v(55.83, -0.02) * mm, "end": v(66.7, -0.02) * mm});
            skLineSegment(sketch, "E176", {"start": v(66.7, -0.02) * mm, "end": v(66.7, 62.57) * mm});
            skLineSegment(sketch, "E177", {"start": v(66.7, 62.57) * mm, "end": v(-76.8, 62.57) * mm});
            skLineSegment(sketch, "E178", {"start": v(-76.8, 62.57) * mm, "end": v(-76.8, 0.14) * mm});
            skLineSegment(sketch, "E179", {"start": v(-55.83, -0.02) * mm, "end": v(-76.8, 0.14) * mm});
            skPoint(sketch, "E180.orphan", {"position": v(-76.8, -0.02) * mm});
            skPoint(sketch, "E181.orphan", {"position": v(-80.06, 0.16) * mm});
            skSolve(sketch);
        }
        {
            var Q0;
            {var subQ0=sQuery(id+"F12.wireOp",EDGE,"E165");Q0=makeQuery(id+"F12.imprint","IMPRINT",FACE,{"disambiguationData":[TD([[makeQuery(id+"F12.imprint","IMPRINT",EDGE,{"derivedFrom":subQ0}),1.0]])]});}
            extrude(context, id + "F14", {"entities" : qUnion([Q0]), "operationType" : NewBodyOperationType.REMOVE, "endBound" : BoundingType.SYMMETRIC, "oppositeDirection" : true, "depth" : 120 * mm, "offsetDistance" : 25 * mm});
        }
        {
            var Q0;
            Q0 = qSketchRegion(id + "F13", true);
            extrude(context, id + "F15", {"entities" : qUnion([Q0]), "operationType" : NewBodyOperationType.REMOVE, "depth" : 25 * mm, "offsetDistance" : 25 * mm});
        }
        {
            var Q0;
            Q0=qCreatedBy(makeId("Top.planeOp"),FACE);
            var sketch = newSketch(context, id + "F16", { "sketchPlane" : qUnion([Q0])});
            skPoint(sketch, "E182.0", {"position": v(36.25, 6.57) * mm});
            skFitSpline(sketch, "E183.0", {"points": [v(55.86, 0) * mm, v(55.12, -0.36) * mm, v(53.54, -1.14) * mm, v(50.22, 0.08) * mm, v(42.97, 2.72) * mm, v(36.22, 6.43) * mm, v(30.55, 10.4) * mm, v(23.62, 13.14) * mm, v(17.07, 13.5) * mm, v(11.77, 12.84) * mm, v(8.14, 10.83) * mm, v(5.88, 9.9) * mm, v(2.8, 9.23) * mm, v(0.92, 9.17) * mm, v(0, 9.15) * mm]});
            skFitSpline(sketch, "E184.0", {"points": [v(-55.86, 0) * mm, v(-55.12, -0.36) * mm, v(-53.54, -1.14) * mm, v(-50.22, 0.08) * mm, v(-42.97, 2.72) * mm, v(-36.22, 6.43) * mm, v(-30.55, 10.4) * mm, v(-23.62, 13.14) * mm, v(-17.07, 13.5) * mm, v(-11.77, 12.84) * mm, v(-8.14, 10.83) * mm, v(-5.88, 9.9) * mm, v(-2.8, 9.23) * mm, v(-0.92, 9.17) * mm, v(0, 9.15) * mm]});
            skFitSpline(sketch, "E185.0", {"points": [v(-48.78, -3.43) * mm, v(-46.2, -2.95) * mm, v(-41.34, -2.03) * mm, v(-35.43, -0.12) * mm, v(-31.43, 1.7) * mm, v(-26.79, 2.75) * mm, v(-21.44, 3.33) * mm, v(-17.79, 3.37) * mm, v(-14.28, 2.77) * mm, v(-10.66, 2.14) * mm, v(-6.82, 1.06) * mm, v(-5.2, 0.7) * mm, v(-3, 0.56) * mm, v(-1.01, 0.6) * mm, v(-0.27, 0.58) * mm, v(0, 0.6) * mm]});
            skFitSpline(sketch, "E186.0", {"points": [v(48.78, -3.43) * mm, v(46.2, -2.95) * mm, v(41.34, -2.03) * mm, v(35.43, -0.12) * mm, v(31.43, 1.7) * mm, v(26.79, 2.75) * mm, v(21.44, 3.33) * mm, v(17.79, 3.37) * mm, v(14.28, 2.77) * mm, v(10.66, 2.14) * mm, v(6.82, 1.06) * mm, v(5.2, 0.7) * mm, v(3, 0.56) * mm, v(1.01, 0.6) * mm, v(0.27, 0.58) * mm, v(0, 0.6) * mm]});
            skFitSpline(sketch, "E187.0", {"points": [v(0, -31.65) * mm, v(-0.93, -31.58) * mm, v(-2.95, -31.44) * mm, v(-6.91, -31.04) * mm, v(-12.57, -29.99) * mm, v(-20.77, -27.37) * mm, v(-28.08, -23.7) * mm, v(-34.59, -18.97) * mm, v(-41.57, -11.7) * mm, v(-46.8, -6.4) * mm, v(-49.06, -5.32) * mm, v(-50, -4.68) * mm, v(-49.72, -3.89) * mm, v(-49.12, -3.6) * mm, v(-48.78, -3.43) * mm]});
            skFitSpline(sketch, "E188.0", {"points": [v(0, -31.65) * mm, v(0.93, -31.58) * mm, v(2.95, -31.44) * mm, v(6.91, -31.04) * mm, v(12.57, -29.99) * mm, v(20.77, -27.37) * mm, v(28.08, -23.7) * mm, v(34.59, -18.97) * mm, v(41.57, -11.7) * mm, v(46.8, -6.4) * mm, v(49.06, -5.32) * mm, v(50, -4.68) * mm, v(49.72, -3.89) * mm, v(49.12, -3.6) * mm, v(48.78, -3.43) * mm]});
            skLineSegment(sketch, "E189.0", {"start": v(55.83, -0.02) * mm, "end": v(60, -0.02) * mm});
            skLineSegment(sketch, "E190.0", {"start": v(60, -3.75) * mm, "end": v(60, -0.02) * mm});
            skLineSegment(sketch, "E190.1", {"start": v(60, -3.78) * mm, "end": v(49.84, -4.6) * mm});
            skLineSegment(sketch, "E191.0", {"start": v(-60, 0.02) * mm, "end": v(-60, -3.75) * mm});
            skLineSegment(sketch, "E191.1", {"start": v(-60, -3.75) * mm, "end": v(-60, -5.21) * mm});
            skLineSegment(sketch, "E191.2", {"start": v(-49.17, -5.21) * mm, "end": v(-60, -5.21) * mm});
            skLineSegment(sketch, "E191.3", {"start": v(-55.83, -0.02) * mm, "end": v(-60, 0.02) * mm});
            skLineSegment(sketch, "E192", {"start": v(49.84, -4.6) * mm, "end": v(49.5, -4.63) * mm});
            skPoint(sketch, "E193.orphan", {"position": v(0, -31.65) * mm});
            skPoint(sketch, "E194.orphan", {"position": v(66.7, -0.02) * mm});
            skLineSegment(sketch, "E195", {"start": v(60, -3.75) * mm, "end": v(60, -3.78) * mm});
            skPoint(sketch, "E196.orphan", {"position": v(71.1, -2.88) * mm});
            skPoint(sketch, "E197.orphan", {"position": v(-76.8, 0.14) * mm});
            skPoint(sketch, "E198.orphan", {"position": v(-68.23, -5.21) * mm});
            skSolve(sketch);
        }
        {
            var Q0;
            Q0 = qSketchRegion(id + "F16", true);
            extrude(context, id + "F17", {"entities" : qUnion([Q0]), "operationType" : NewBodyOperationType.REMOVE, "endBound" : BoundingType.THROUGH_ALL, "depth" : 6 * mm, "offsetDistance" : 25 * mm});
        }
        {
            var Q0;
            Q0=qCreatedBy(makeId("Top.planeOp"),FACE);
            var sketch = newSketch(context, id + "F18", { "sketchPlane" : qUnion([Q0])});
            skFitSpline(sketch, "E199.1.1", {"points": [v(-55.83, -0.02) * mm, v(-55.9, 0.1) * mm, v(-55.98, 0.33) * mm, v(-55.98, 0.65) * mm, v(-55.94, 0.9) * mm, v(-55.88, 1.07) * mm, v(-55.8, 1.24) * mm, v(-55.65, 1.44) * mm, v(-55.43, 1.65) * mm, v(-55.13, 1.87) * mm, v(-54.81, 2.06) * mm, v(-54.4, 2.32) * mm, v(-53.86, 2.63) * mm, v(-53.23, 3) * mm, v(-52.6, 3.38) * mm, v(-52.2, 3.62) * mm, v(-51.99, 3.75) * mm]});
            skFitSpline(sketch, "E199.2.2", {"points": [v(-51.99, 3.75) * mm, v(-51.58, 4) * mm, v(-50.77, 4.51) * mm, v(-49.6, 5.38) * mm, v(-48.46, 6.3) * mm, v(-47.34, 7.25) * mm, v(-46.22, 8.22) * mm, v(-45.12, 9.22) * mm, v(-44.09, 10.23) * mm, v(-43.44, 10.9) * mm, v(-43.13, 11.25) * mm]});
            skFitSpline(sketch, "E199.3.2", {"points": [v(-43.13, 11.25) * mm, v(-42.87, 11.54) * mm, v(-42.34, 12.14) * mm, v(-41.54, 13.1) * mm, v(-40.73, 14.06) * mm, v(-39.92, 15.02) * mm, v(-39.23, 15.83) * mm, v(-38.67, 16.46) * mm, v(-37.84, 17.4) * mm, v(-37.16, 18.16) * mm, v(-36.65, 18.75) * mm]});
            skFitSpline(sketch, "E199.3.4", {"points": [v(36.65, 18.75) * mm, v(37.16, 18.16) * mm, v(37.84, 17.4) * mm, v(38.67, 16.46) * mm, v(39.23, 15.83) * mm, v(39.92, 15.02) * mm, v(40.73, 14.06) * mm, v(41.54, 13.1) * mm, v(42.34, 12.14) * mm, v(42.87, 11.54) * mm, v(43.13, 11.25) * mm]});
            skFitSpline(sketch, "E199.4.0", {"points": [v(-36.65, 18.75) * mm, v(-36.4, 19.05) * mm, v(-35.88, 19.66) * mm, v(-35.08, 20.63) * mm, v(-34.29, 21.6) * mm, v(-33.48, 22.58) * mm, v(-32.78, 23.38) * mm, v(-32.2, 24.01) * mm, v(-31.64, 24.63) * mm, v(-30.93, 25.38) * mm, v(-30.37, 25.96) * mm, v(-30.1, 26.25) * mm]});
            skFitSpline(sketch, "E199.4.2", {"points": [v(30.1, 26.25) * mm, v(30.37, 25.96) * mm, v(30.93, 25.38) * mm, v(31.64, 24.63) * mm, v(32.2, 24.01) * mm, v(32.78, 23.38) * mm, v(33.48, 22.58) * mm, v(34.29, 21.6) * mm, v(35.08, 20.63) * mm, v(35.88, 19.66) * mm, v(36.4, 19.05) * mm, v(36.65, 18.75) * mm]});
            skFitSpline(sketch, "E199.5.1", {"points": [v(-30.1, 26.25) * mm, v(-29.64, 26.73) * mm, v(-28.93, 27.46) * mm, v(-27.9, 28.42) * mm, v(-27.09, 29.12) * mm, v(-26.25, 29.78) * mm, v(-25.1, 30.62) * mm, v(-23.64, 31.6) * mm, v(-22.1, 32.5) * mm, v(-20.85, 33.12) * mm, v(-20.06, 33.47) * mm, v(-19.41, 33.71) * mm, v(-18.92, 33.88) * mm, v(-18.42, 34.03) * mm, v(-17.76, 34.23) * mm, v(-16.92, 34.46) * mm, v(-15.9, 34.7) * mm, v(-15, 34.81) * mm, v(-14.3, 34.87) * mm, v(-13.59, 34.9) * mm, v(-12.7, 34.91) * mm, v(-11.64, 34.84) * mm, v(-10.58, 34.7) * mm, v(-9.7, 34.56) * mm, v(-9.01, 34.41) * mm, v(-8.5, 34.3) * mm, v(-8, 34.16) * mm, v(-7.34, 33.93) * mm, v(-6.55, 33.57) * mm, v(-5.61, 33.09) * mm, v(-4.68, 32.6) * mm, v(-3.78, 32.03) * mm, v(-3.07, 31.5) * mm, v(-2.49, 31.08) * mm, v(-2.04, 30.78) * mm, v(-1.58, 30.5) * mm, v(-1.16, 30.33) * mm, v(-0.82, 30.25) * mm, v(-0.45, 30.21) * mm, v(-0.18, 30.23) * mm, v(0, 30.25) * mm]});
            skFitSpline(sketch, "E199.5.2", {"points": [v(0, 30.25) * mm, v(0.18, 30.23) * mm, v(0.45, 30.21) * mm, v(0.82, 30.25) * mm, v(1.16, 30.33) * mm, v(1.58, 30.5) * mm, v(2.04, 30.78) * mm, v(2.49, 31.08) * mm, v(3.07, 31.5) * mm, v(3.78, 32.03) * mm, v(4.68, 32.6) * mm, v(5.61, 33.09) * mm, v(6.55, 33.57) * mm, v(7.34, 33.93) * mm, v(8, 34.16) * mm, v(8.5, 34.3) * mm, v(9.01, 34.41) * mm, v(9.7, 34.56) * mm, v(10.58, 34.7) * mm, v(11.64, 34.84) * mm, v(12.7, 34.91) * mm, v(13.59, 34.9) * mm, v(14.3, 34.87) * mm, v(15, 34.81) * mm, v(15.9, 34.7) * mm, v(16.92, 34.46) * mm, v(17.76, 34.23) * mm, v(18.42, 34.03) * mm, v(18.92, 33.88) * mm, v(19.41, 33.71) * mm, v(20.06, 33.47) * mm, v(20.85, 33.12) * mm, v(22.1, 32.5) * mm, v(23.64, 31.6) * mm, v(25.1, 30.62) * mm, v(26.25, 29.78) * mm, v(27.09, 29.12) * mm, v(27.9, 28.42) * mm, v(28.93, 27.46) * mm, v(29.64, 26.73) * mm, v(30.1, 26.25) * mm]});
            skFitSpline(sketch, "E199.6.3", {"points": [v(43.13, 11.25) * mm, v(43.44, 10.9) * mm, v(44.09, 10.23) * mm, v(45.12, 9.22) * mm, v(46.22, 8.22) * mm, v(47.34, 7.25) * mm, v(48.46, 6.3) * mm, v(49.6, 5.38) * mm, v(50.77, 4.51) * mm, v(51.58, 4) * mm, v(51.99, 3.75) * mm]});
            skFitSpline(sketch, "E199.7.0", {"points": [v(51.99, 3.75) * mm, v(52.2, 3.62) * mm, v(52.6, 3.38) * mm, v(53.23, 3) * mm, v(53.86, 2.63) * mm, v(54.4, 2.32) * mm, v(54.81, 2.06) * mm, v(55.13, 1.87) * mm, v(55.43, 1.65) * mm, v(55.65, 1.44) * mm, v(55.8, 1.24) * mm, v(55.88, 1.07) * mm, v(55.94, 0.9) * mm, v(55.98, 0.65) * mm, v(55.98, 0.33) * mm, v(55.9, 0.1) * mm, v(55.83, -0.02) * mm]});
            skFitSpline(sketch, "E199.9.1", {"points": [v(-42.04, -11.25) * mm, v(-42.35, -10.93) * mm, v(-42.99, -10.27) * mm, v(-43.98, -9.28) * mm, v(-44.85, -8.43) * mm, v(-45.55, -7.77) * mm, v(-46.09, -7.3) * mm, v(-46.64, -6.83) * mm, v(-47.2, -6.39) * mm, v(-47.7, -6.05) * mm, v(-48.12, -5.8) * mm, v(-48.44, -5.62) * mm, v(-48.76, -5.45) * mm, v(-49.07, -5.27) * mm, v(-49.38, -5.1) * mm, v(-49.63, -4.92) * mm, v(-49.79, -4.74) * mm, v(-49.86, -4.58) * mm, v(-49.87, -4.41) * mm, v(-49.82, -4.25) * mm, v(-49.75, -4.1) * mm, v(-49.6, -3.92) * mm, v(-49.47, -3.81) * mm, v(-49.37, -3.75) * mm]});
            skFitSpline(sketch, "E199.9.3", {"points": [v(49.37, -3.75) * mm, v(49.47, -3.81) * mm, v(49.65, -3.95) * mm, v(49.8, -4.2) * mm, v(49.87, -4.4) * mm, v(49.86, -4.58) * mm, v(49.79, -4.74) * mm, v(49.67, -4.87) * mm, v(49.53, -4.99) * mm, v(49.34, -5.12) * mm, v(49.08, -5.27) * mm, v(48.76, -5.45) * mm, v(48.44, -5.62) * mm, v(48.13, -5.8) * mm, v(47.71, -6.05) * mm, v(47.21, -6.39) * mm, v(46.64, -6.83) * mm, v(46.1, -7.3) * mm, v(45.55, -7.77) * mm, v(44.85, -8.43) * mm, v(43.98, -9.27) * mm, v(42.99, -10.27) * mm, v(42.35, -10.93) * mm, v(42.04, -11.25) * mm]});
            skFitSpline(sketch, "E199.10.1", {"points": [v(42.04, -11.25) * mm, v(41.44, -11.87) * mm, v(40.67, -12.66) * mm, v(39.71, -13.64) * mm, v(39.06, -14.3) * mm, v(38.25, -15.12) * mm, v(37.28, -16.08) * mm, v(36.3, -17.04) * mm, v(35.3, -17.96) * mm, v(34.65, -18.55) * mm, v(34.33, -18.84) * mm]});
            skFitSpline(sketch, "E199.10.3", {"points": [v(-34.33, -18.84) * mm, v(-34.65, -18.55) * mm, v(-35.3, -17.96) * mm, v(-36.3, -17.04) * mm, v(-37.28, -16.08) * mm, v(-38.25, -15.12) * mm, v(-39.06, -14.3) * mm, v(-39.71, -13.64) * mm, v(-40.67, -12.66) * mm, v(-41.44, -11.87) * mm, v(-42.04, -11.25) * mm]});
            skFitSpline(sketch, "E199.11.1", {"points": [v(34.33, -18.84) * mm, v(33.92, -19.2) * mm, v(33.09, -19.9) * mm, v(32, -20.77) * mm, v(31.08, -21.44) * mm, v(30.15, -22.1) * mm, v(28.97, -22.9) * mm, v(27.53, -23.79) * mm, v(25.58, -24.9) * mm, v(24.09, -25.65) * mm, v(23.08, -26.12) * mm]});
            skFitSpline(sketch, "E199.11.3", {"points": [v(-23.08, -26.12) * mm, v(-24.09, -25.65) * mm, v(-25.58, -24.9) * mm, v(-27.53, -23.79) * mm, v(-28.97, -22.9) * mm, v(-30.15, -22.1) * mm, v(-31.08, -21.44) * mm, v(-32, -20.77) * mm, v(-33.09, -19.9) * mm, v(-33.92, -19.2) * mm, v(-34.33, -18.84) * mm]});
            skFitSpline(sketch, "E199.12.0", {"points": [v(23.08, -26.12) * mm, v(22.2, -26.53) * mm, v(20.38, -27.31) * mm, v(18.05, -28.17) * mm, v(16.16, -28.8) * mm, v(14.24, -29.39) * mm, v(11.83, -30.04) * mm, v(8.9, -30.67) * mm, v(4.98, -31.28) * mm, v(2, -31.5) * mm, v(0, -31.65) * mm]});
            skFitSpline(sketch, "E199.12.1", {"points": [v(0, -31.65) * mm, v(-2, -31.5) * mm, v(-4.98, -31.28) * mm, v(-8.9, -30.67) * mm, v(-11.83, -30.04) * mm, v(-14.24, -29.39) * mm, v(-16.16, -28.8) * mm, v(-18.05, -28.17) * mm, v(-20.38, -27.31) * mm, v(-22.2, -26.53) * mm, v(-23.08, -26.12) * mm]});
            skPoint(sketch, "E199.3.7.end.orphan", {"position": v(-8.85, 11.25) * mm});
            skPoint(sketch, "E199.2.3.end.orphan", {"position": v(-28.15, 11.25) * mm});
            skPoint(sketch, "E199.3.6.end.orphan", {"position": v(8.85, 11.25) * mm});
            skPoint(sketch, "E199.6.2.start.orphan", {"position": v(28.15, 11.25) * mm});
            skPoint(sketch, "E199.8.2.end.orphan", {"position": v(0, 0.6) * mm});
            skPoint(sketch, "E199.7.1.end.orphan", {"position": v(41.3, 3.75) * mm});
            skPoint(sketch, "E199.1.0.start.orphan", {"position": v(-41.3, 3.75) * mm});
            skLineSegment(sketch, "E200", {"start": v(-55.83, -0.02) * mm, "end": v(-49.6, -4.93) * mm});
            skPoint(sketch, "E199.8.1.end.orphan", {"position": v(-48.78, -3.43) * mm});
            skPoint(sketch, "E199.8.1.start.orphan", {"position": v(-49.37, -3.75) * mm});
            skLineSegment(sketch, "E201", {"start": v(55.83, -0.02) * mm, "end": v(48.9, -5.37) * mm});
            skPoint(sketch, "E199.8.4.end.orphan", {"position": v(49.37, -3.75) * mm});
            skPoint(sketch, "E199.8.4.start.orphan", {"position": v(48.78, -3.43) * mm});
            skSolve(sketch);
        }
        {
            var Q0;
            Q0 = qSketchRegion(id + "F18", true);
            extrude(context, id + "F19", {"entities" : qUnion([Q0]), "depth" : 5 * mm, "offsetDistance" : 25 * mm});
        }
    });
